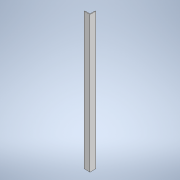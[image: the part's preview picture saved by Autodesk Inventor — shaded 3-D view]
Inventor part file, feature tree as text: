
AUTODESK INVENTOR PART (.ipt)
format: ipt  version: 2022 (Build 260153000, 153)  size: 98,304 bytes
history: native  units: mm
features: extrude x1, sketch x1
ambient origin geometry x8: Origin, YZ Plane, XZ Plane, XY Plane, X Axis, Y Axis, Z Axis, Center Point
bodies: Solid1 (feature_tree)
feature tree (2):
  extrude  "Extrusion1"  Depth=50.0mm
  sketch  "Sketch1"  dims[d0=50.0mm d1=50.0mm d2=5.0mm d3=5.0mm d4=1200.0mm d5=0.0mm]
